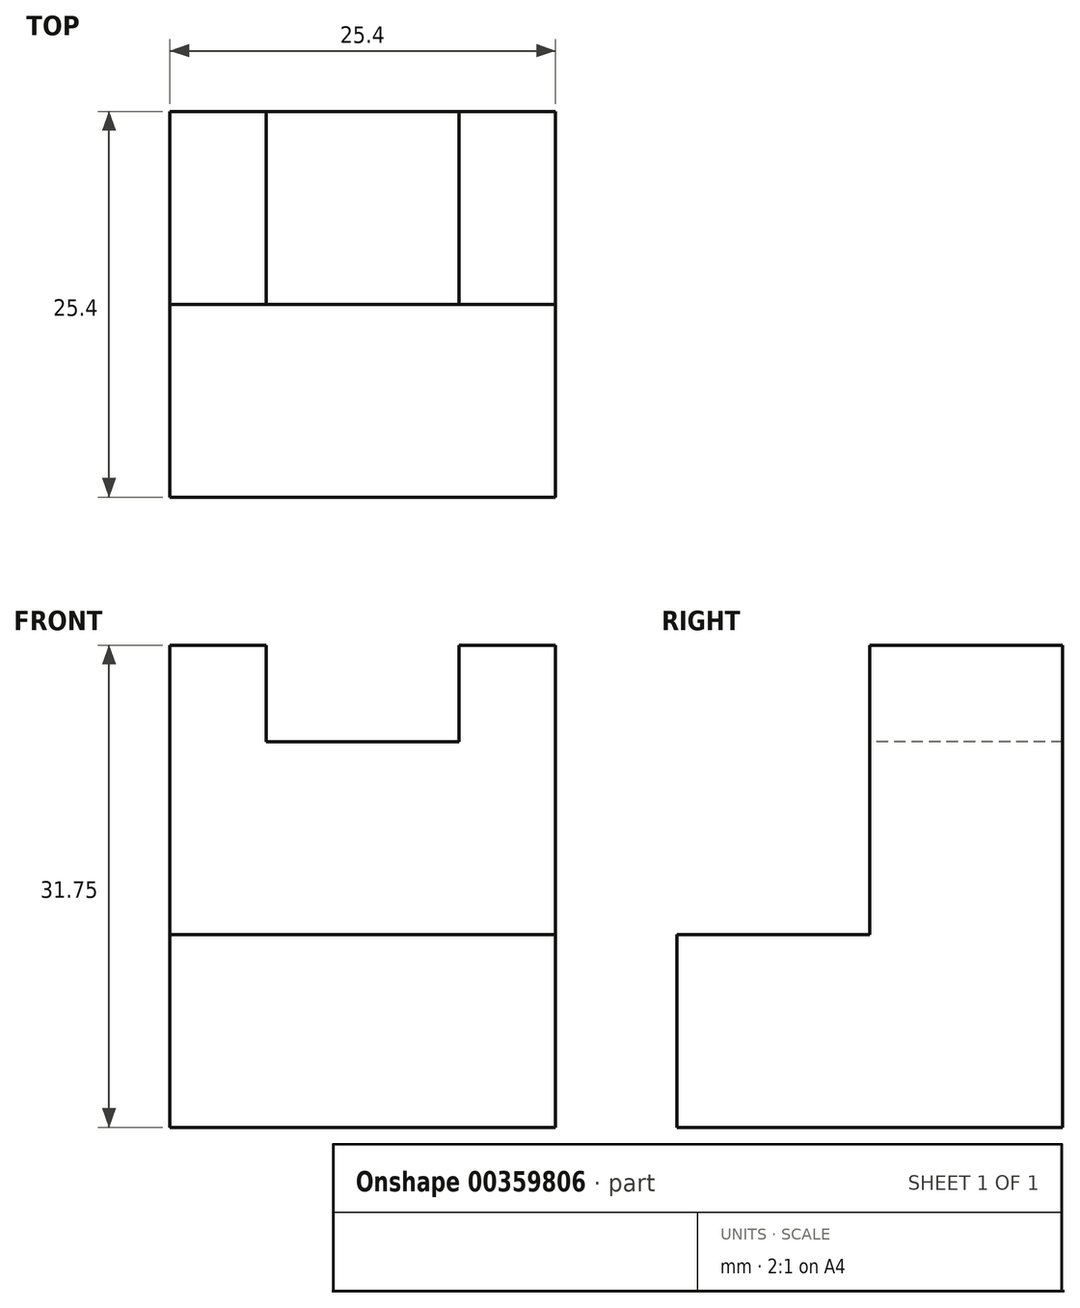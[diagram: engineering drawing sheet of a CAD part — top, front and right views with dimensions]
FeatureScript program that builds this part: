
annotation { "Feature Type Name" : "Feature", "Feature Type Description" : "" }
export const myFeature = defineFeature(function(context is Context, id is Id, definition is map)
    precondition{}
    {
        {
            var Q0;
            Q0=qCreatedBy(makeId("Right.planeOp"),FACE);
            var sketch = newSketch(context, id + "F0", { "sketchPlane" : qUnion([Q0])});
            skLineSegment(sketch, "E0", {"start": v(0, 0) * mm, "end": v(-12.7, 0) * mm});
            skLineSegment(sketch, "E1", {"start": v(-12.7, 0) * mm, "end": v(-12.7, -12.7) * mm});
            skLineSegment(sketch, "E2", {"start": v(-12.7, -12.7) * mm, "end": v(12.7, -12.7) * mm});
            skLineSegment(sketch, "E3", {"start": v(12.7, -12.7) * mm, "end": v(12.7, 19.05) * mm});
            skLineSegment(sketch, "E4", {"start": v(12.7, 19.05) * mm, "end": v(0, 19.05) * mm});
            skLineSegment(sketch, "E5", {"start": v(0, 19.05) * mm, "end": v(0, 0) * mm});
            skSolve(sketch);
        }
        {
            var Q0;
            Q0 = qSketchRegion(id + "F0", true);
            extrude(context, id + "F1", {"entities" : qUnion([Q0]), "depth" : 25.4 * mm});
        }
        {
            var Q0;
            Q0=makeQuery(id+"F1.opExtrude","SWEPT_FACE",FACE,{"disambiguationData":[OSD([sQuery(id+"F0.wireOp",EDGE,"E5")])]});
            var sketch = newSketch(context, id + "F2", { "sketchPlane" : qUnion([Q0])});
            skLineSegment(sketch, "E6", {"start": v(6.35, 19.05) * mm, "end": v(6.35, 12.7) * mm});
            skLineSegment(sketch, "E7", {"start": v(6.35, 12.7) * mm, "end": v(19.05, 12.7) * mm});
            skLineSegment(sketch, "E8", {"start": v(19.05, 12.7) * mm, "end": v(19.05, 19.05) * mm});
            skSolve(sketch);
        }
        {
            var Q0;
            {var subQ0=sQuery(id+"F2.wireOp",EDGE,"E6");Q0=makeQuery(id+"F2.imprint","IMPRINT",FACE,{"disambiguationData":[TD([[makeQuery(id+"F2.imprint","IMPRINT",EDGE,{"derivedFrom":subQ0}),1.0]])]});}
            extrude(context, id + "F3", {"entities" : qUnion([Q0]), "operationType" : NewBodyOperationType.REMOVE, "oppositeDirection" : true, "depth" : 25.4 * mm});
        }
    });
